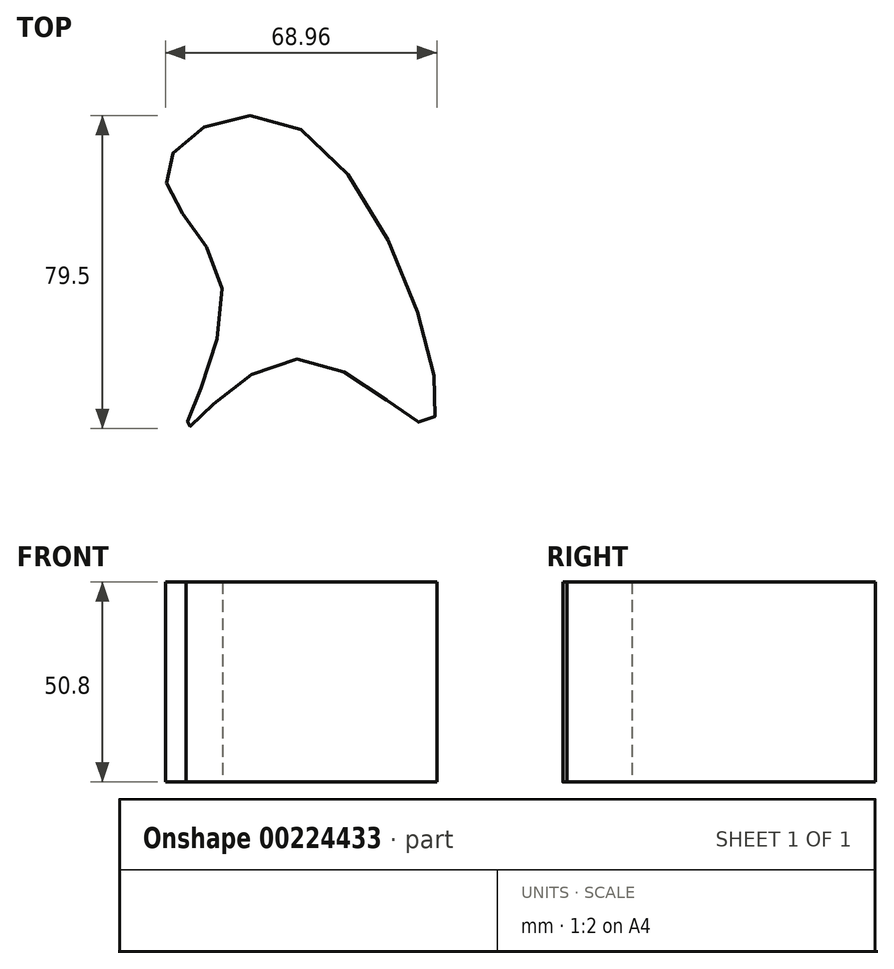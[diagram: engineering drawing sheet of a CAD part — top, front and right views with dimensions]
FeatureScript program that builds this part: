
annotation { "Feature Type Name" : "Feature", "Feature Type Description" : "" }
export const myFeature = defineFeature(function(context is Context, id is Id, definition is map)
    precondition{}
    {
        {
            var Q0;
            Q0=qCreatedBy(makeId("Top.planeOp"),FACE);
            var sketch = newSketch(context, id + "F0", { "sketchPlane" : qUnion([Q0])});
            skFitSpline(sketch, "E0", {"points": [v(-19.52, 0) * mm, v(-28.56, -35.55) * mm, v(0, -17.92) * mm, v(33.72, -34.06) * mm, v(0, 40.73) * mm, v(-33.85, 29.92) * mm, v(-19.52, 0) * mm]});
            skSolve(sketch);
        }
        {
            var Q0;
            Q0=makeQuery(id+"F0.imprint","IMPRINT",FACE,{"disambiguationData":[TD([[makeQuery(id+"F0.imprint","IMPRINT",EDGE,{"derivedFrom":sQuery(id+"F0.wireOp",EDGE,"E0")}),1.0]])]});
            extrude(context, id + "F1", {"entities" : qUnion([Q0]), "depth" : 50.8 * mm});
        }
    });
